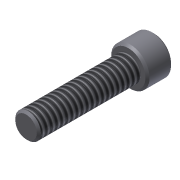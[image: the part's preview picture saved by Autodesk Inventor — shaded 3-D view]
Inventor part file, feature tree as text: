
AUTODESK INVENTOR PART (.ipt)
format: ipt  version: 2011 (Build 150239000, 239)  size: 108,032 bytes
history: native  units: in
note: dims shown in document units (in); Inventor stores cm internally (conversion verified against a paired STEP export)
features: extrude x3, sketch x3, chamfer x1, thread x1
ambient origin geometry x8: Origin, YZ Plane, XZ Plane, XY Plane, X Axis, Y Axis, Z Axis, Center Point
bodies: Solid1 (feature_tree)
feature tree (8):
  extrude  "Extrusion1"  Depth=1.0in TaperAngle=0.0deg
  extrude  "Extrusion2"  Depth=0.25in TaperAngle=0.0deg
  extrude  "Extrusion3"  Depth=0.125in TaperAngle=0.0deg
  chamfer  "Chamfer1"  Distance=0.02in Angle=45.0deg
  thread  "Thread1"  [1 undecoded]
  sketch  "Sketch1"  dims[d0=0.25in d1=1.0in d2=0.0in]
  sketch  "Sketch2"  dims[d3=0.375in d4=0.25in d5=0.0in]
  sketch  "Sketch3"  dims[d6=0.1875in d7=0.125in d8=0.0in d9=0.02in d10=0.125in d11=45.0deg d12=1.0in d13=0.0in]
note: 1 required parameter value undecoded (feature->parameter linkage not recoverable at this tier; creation-order binding heuristic only, values carry confidence <= 0.55)
